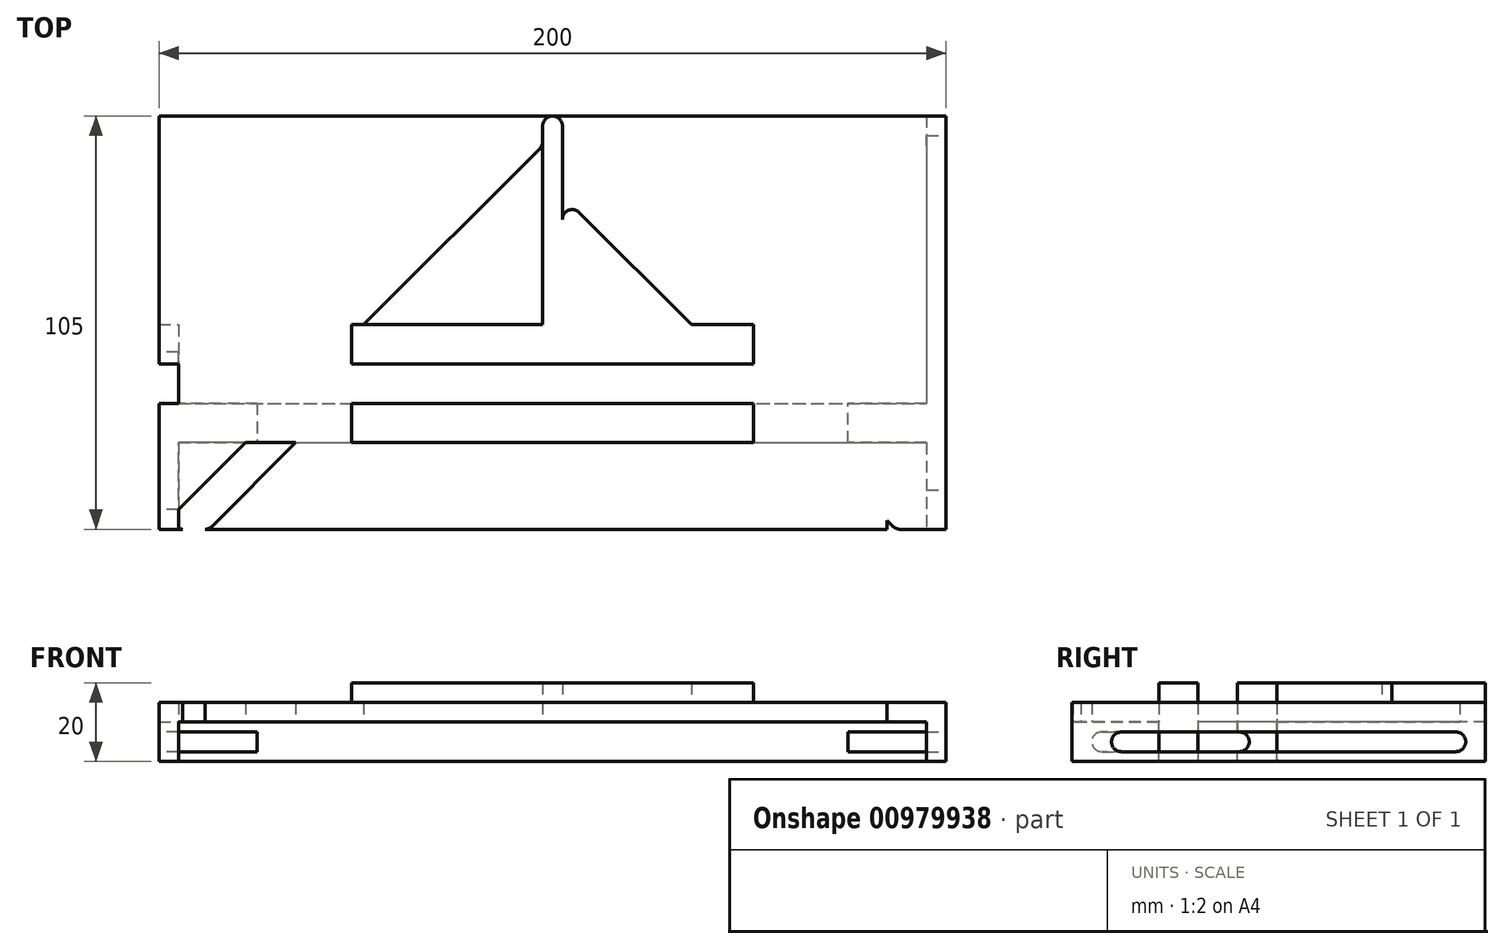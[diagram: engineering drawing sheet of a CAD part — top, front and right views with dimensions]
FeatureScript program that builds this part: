
annotation { "Feature Type Name" : "Feature", "Feature Type Description" : "" }
export const myFeature = defineFeature(function(context is Context, id is Id, definition is map)
    precondition{}
    {
        {
            var Q0;
            Q0=qCreatedBy(makeId("Top.planeOp"),FACE);
            var sketch = newSketch(context, id + "F0", { "sketchPlane" : qUnion([Q0])});
            skLineSegment(sketch, "E0.bottom", {"start": v(-100, 52.5) * mm, "end": v(100, 52.5) * mm});
            skLineSegment(sketch, "E0.top", {"start": v(-100, -52.5) * mm, "end": v(100, -52.5) * mm});
            skLineSegment(sketch, "E0.left", {"start": v(-100, 52.5) * mm, "end": v(-100, -52.5) * mm});
            skLineSegment(sketch, "E0.right", {"start": v(100, 52.5) * mm, "end": v(100, -52.5) * mm});
            skLineSegment(sketch, "E1", {"start": v(95, 52.5) * mm, "end": v(95, -52.5) * mm});
            skLineSegment(sketch, "E2.bottom", {"start": v(0, 52.5) * mm, "end": v(0, 52.5) * mm});
            skLineSegment(sketch, "E2.top", {"start": v(0, -52.5) * mm, "end": v(0, -52.5) * mm});
            skLineSegment(sketch, "E2.left", {"start": v(2.5, 50) * mm, "end": v(2.5, -50) * mm});
            skLineSegment(sketch, "E2.right", {"start": v(-2.5, 50) * mm, "end": v(-2.5, -50) * mm});
            skPoint(sketch, "E3.visualSharp", {"position": v(-2.5, 52.5) * mm});
            skArc(sketch, "E3.filletArc", {"start": v(0, 52.5) * mm, "mid": v(-1.77, 51.77) * mm, "end": v(-2.5, 50) * mm});
            skPoint(sketch, "E4.visualSharp", {"position": v(2.5, 52.5) * mm});
            skArc(sketch, "E4.filletArc", {"start": v(2.5, 50) * mm, "mid": v(1.77, 51.77) * mm, "end": v(0, 52.5) * mm});
            skPoint(sketch, "E5.visualSharp", {"position": v(-2.5, -52.5) * mm});
            skArc(sketch, "E5.filletArc", {"start": v(-2.5, -50) * mm, "mid": v(-1.77, -51.77) * mm, "end": v(0, -52.5) * mm});
            skPoint(sketch, "E6.visualSharp", {"position": v(2.5, -52.5) * mm});
            skArc(sketch, "E6.filletArc", {"start": v(0, -52.5) * mm, "mid": v(1.77, -51.77) * mm, "end": v(2.5, -50) * mm});
            skLineSegment(sketch, "E7", {"start": v(-95.73, -48.23) * mm, "end": v(-3.23, 44.27) * mm});
            skLineSegment(sketch, "E8.0", {"start": v(-86.54, -51.77) * mm, "end": v(-6.77, 28) * mm});
            skLineSegment(sketch, "E9", {"start": v(-2.5, 32.27) * mm, "end": v(-2.5, 0) * mm});
            skLineSegment(sketch, "E10", {"start": v(-2.5, 0) * mm, "end": v(-2.5, 26.24) * mm});
            skPoint(sketch, "E11.visualSharp", {"position": v(-2.5, 32.27) * mm});
            skArc(sketch, "E11.filletArc", {"start": v(-2.5, 26.24) * mm, "mid": v(-4.04, 28.55) * mm, "end": v(-6.77, 28) * mm});
            skLineSegment(sketch, "E12", {"start": v(-2.5, 50) * mm, "end": v(-2.5, 46.04) * mm});
            skPoint(sketch, "E13.visualSharp", {"position": v(-2.5, 45) * mm});
            skArc(sketch, "E13.filletArc", {"start": v(-3.23, 44.27) * mm, "mid": v(-2.7, 45.08) * mm, "end": v(-2.5, 46.04) * mm});
            skLineSegment(sketch, "E14", {"start": v(-93.96, -52.5) * mm, "end": v(-88.3, -52.5) * mm});
            skPoint(sketch, "E15.visualSharp", {"position": v(-100, -52.5) * mm});
            skArc(sketch, "E15.filletArc", {"start": v(-95.73, -48.23) * mm, "mid": v(-96.27, -50.96) * mm, "end": v(-93.96, -52.5) * mm});
            skPoint(sketch, "E16.visualSharp", {"position": v(-87.27, -52.5) * mm});
            skArc(sketch, "E16.filletArc", {"start": v(-88.3, -52.5) * mm, "mid": v(-87.35, -52.3) * mm, "end": v(-86.54, -51.77) * mm});
            skArc(sketch, "E17.MirrorCS", {"start": v(95.73, -48.23) * mm, "mid": v(96.27, -50.96) * mm, "end": v(93.96, -52.5) * mm});
            skLineSegment(sketch, "E18.MirrorCS", {"start": v(93.96, -52.5) * mm, "end": v(88.3, -52.5) * mm});
            skArc(sketch, "E19.MirrorCS", {"start": v(88.3, -52.5) * mm, "mid": v(87.35, -52.3) * mm, "end": v(86.54, -51.77) * mm});
            skLineSegment(sketch, "E20.MirrorCS", {"start": v(95.73, -48.23) * mm, "end": v(3.23, 44.27) * mm});
            skLineSegment(sketch, "E21.MirrorCS", {"start": v(86.54, -51.77) * mm, "end": v(6.77, 28) * mm});
            skArc(sketch, "E22.MirrorCS", {"start": v(2.5, 26.24) * mm, "mid": v(4.04, 28.55) * mm, "end": v(6.77, 28) * mm});
            skArc(sketch, "E23.MirrorCS", {"start": v(3.23, 44.27) * mm, "mid": v(2.7, 45.08) * mm, "end": v(2.5, 46.04) * mm});
            skLineSegment(sketch, "E24", {"start": v(-3.23, 44.27) * mm, "end": v(0, 47.5) * mm, "construction": true});
            skLineSegment(sketch, "E25", {"start": v(3.23, 44.27) * mm, "end": v(0, 47.5) * mm, "construction": true});
            skLineSegment(sketch, "E26.bottom", {"start": v(-48, 65.5) * mm, "end": v(48, 65.5) * mm, "construction": true});
            skLineSegment(sketch, "E26.top", {"start": v(-48, -30.5) * mm, "end": v(48, -30.5) * mm, "construction": true});
            skLineSegment(sketch, "E26.left", {"start": v(-48, 65.5) * mm, "end": v(-48, -30.5) * mm, "construction": true});
            skLineSegment(sketch, "E26.right", {"start": v(48, 65.5) * mm, "end": v(48, -30.5) * mm, "construction": true});
            skLineSegment(sketch, "E27", {"start": v(-48, -25.5) * mm, "end": v(48, -25.5) * mm, "construction": true});
            skLineSegment(sketch, "E28", {"start": v(-48, 2.5) * mm, "end": v(48, 2.5) * mm, "construction": true});
            skLineSegment(sketch, "E29", {"start": v(-48, -0.5) * mm, "end": v(48, -0.5) * mm, "construction": true});
            skLineSegment(sketch, "E30.bottom", {"start": v(-100, -0.5) * mm, "end": v(100, -0.5) * mm});
            skLineSegment(sketch, "E30.top", {"start": v(-100, -30.5) * mm, "end": v(100, -30.5) * mm});
            skLineSegment(sketch, "E30.left", {"start": v(-100, -0.5) * mm, "end": v(-100, -30.5) * mm});
            skLineSegment(sketch, "E30.right", {"start": v(100, -0.5) * mm, "end": v(100, -30.5) * mm});
            skLineSegment(sketch, "E31", {"start": v(-95, -0.5) * mm, "end": v(-95, -30.5) * mm});
            skLineSegment(sketch, "E32", {"start": v(-100, -10.5) * mm, "end": v(100, -10.5) * mm});
            skLineSegment(sketch, "E33", {"start": v(-100, -20.5) * mm, "end": v(100, -20.5) * mm});
            skLineSegment(sketch, "E34", {"start": v(-51, -0.5) * mm, "end": v(-51, -10.5) * mm});
            skLineSegment(sketch, "E35", {"start": v(-51, -10.5) * mm, "end": v(-51, -20.5) * mm, "construction": true});
            skLineSegment(sketch, "E36", {"start": v(-51, -20.5) * mm, "end": v(-51, -30.5) * mm});
            skLineSegment(sketch, "E37", {"start": v(51, -0.5) * mm, "end": v(51, -10.5) * mm});
            skLineSegment(sketch, "E38", {"start": v(51, -10.5) * mm, "end": v(51, -20.5) * mm, "construction": true});
            skLineSegment(sketch, "E39", {"start": v(51, -20.5) * mm, "end": v(51, -30.5) * mm});
            skLineSegment(sketch, "E40", {"start": v(85, 52.5) * mm, "end": v(85, -52.5) * mm});
            skLineSegment(sketch, "E41", {"start": v(-95, -30.5) * mm, "end": v(-95, -52.5) * mm});
            skSolve(sketch);
        }
        {
            var Q0;
            {var subQ0=sQuery(id+"F0.wireOp",EDGE,"E0.right");var subQ1=sQuery(id+"F0.wireOp",EDGE,"E0.bottom");var subQ2=makeQuery(id+"F0.imprint","INTERSECT",VERTEX,{"derivedFrom":[subQ1,subQ0]});Q0=makeQuery(id+"F0.imprint","IMPRINT",FACE,{"disambiguationData":[TD([[makeQuery(id+"F0.imprint","IMPRINT",EDGE,{"disambiguationData":[TD([[subQ2,1.0]])],"derivedFrom":subQ1}),-1.0]])]});}
            var Q1;
            {var subQ10=sQuery(id+"F0.wireOp",EDGE,"E3.filletArc");Q1=makeQuery(id+"F0.imprint","IMPRINT",FACE,{"disambiguationData":[TD([[makeQuery(id+"F0.imprint","IMPRINT",EDGE,{"derivedFrom":subQ10}),-1.0]])]});}
            var Q2;
            {var subQ0=sQuery(id+"F0.wireOp",EDGE,"E4.filletArc");Q2=makeQuery(id+"F0.imprint","IMPRINT",FACE,{"disambiguationData":[TD([[makeQuery(id+"F0.imprint","IMPRINT",EDGE,{"derivedFrom":subQ0}),-1.0]])]});}
            var Q3;
            Q3=makeQuery(id+"F0.imprint","IMPRINT",FACE,{"disambiguationData":[TD([[makeQuery(id+"F0.imprint","IMPRINT",EDGE,{"derivedFrom":sQuery(id+"F0.wireOp",EDGE,"E3.filletArc")}),1.0]])]});
            var Q4;
            {var subQ0=sQuery(id+"F0.wireOp",EDGE,"E9");Q4=makeQuery(id+"F0.imprint","IMPRINT",FACE,{"disambiguationData":[TD([[makeQuery(id+"F0.imprint","IMPRINT",EDGE,{"derivedFrom":subQ0}),-1.0]])]});}
            var Q5;
            {var subQ1=sQuery(id+"F0.wireOp",EDGE,"E10");Q5=makeQuery(id+"F0.imprint","IMPRINT",FACE,{"disambiguationData":[TD([[makeQuery(id+"F0.imprint","IMPRINT",EDGE,{"derivedFrom":subQ1}),1.0]])]});}
            var Q6;
            {var subQ0=sQuery(id+"F0.wireOp",EDGE,"E22.MirrorCS");Q6=makeQuery(id+"F0.imprint","IMPRINT",FACE,{"disambiguationData":[TD([[makeQuery(id+"F0.imprint","IMPRINT",EDGE,{"derivedFrom":subQ0}),-1.0]])]});}
            var Q7;
            {var subQ0=sQuery(id+"F0.wireOp",EDGE,"E22.MirrorCS");Q7=makeQuery(id+"F0.imprint","IMPRINT",FACE,{"disambiguationData":[TD([[makeQuery(id+"F0.imprint","IMPRINT",EDGE,{"derivedFrom":subQ0}),1.0]])]});}
            var Q8;
            {var subQ0=sQuery(id+"F0.wireOp",EDGE,"E1");var subQ1=sQuery(id+"F0.wireOp",EDGE,"E0.bottom");var subQ2=makeQuery(id+"F0.imprint","INTERSECT",VERTEX,{"derivedFrom":[subQ1,subQ0]});Q8=makeQuery(id+"F0.imprint","IMPRINT",FACE,{"disambiguationData":[TD([[makeQuery(id+"F0.imprint","IMPRINT",EDGE,{"disambiguationData":[TD([[subQ2,1.0]])],"derivedFrom":subQ1}),-1.0]])]});}
            var Q9;
            {var subQ0=sQuery(id+"F0.wireOp",EDGE,"E30.bottom");var subQ1=sQuery(id+"F0.wireOp",EDGE,"E1");var subQ2=makeQuery(id+"F0.imprint","INTERSECT",VERTEX,{"derivedFrom":[subQ1,subQ0]});Q9=makeQuery(id+"F0.imprint","IMPRINT",FACE,{"disambiguationData":[TD([[makeQuery(id+"F0.imprint","IMPRINT",EDGE,{"disambiguationData":[TD([[subQ2,-1.0]])],"derivedFrom":subQ1}),-1.0]])]});}
            var Q10;
            {var subQ0=sQuery(id+"F0.wireOp",EDGE,"E32");var subQ1=sQuery(id+"F0.wireOp",EDGE,"E1");var subQ2=makeQuery(id+"F0.imprint","INTERSECT",VERTEX,{"derivedFrom":[subQ1,subQ0]});Q10=makeQuery(id+"F0.imprint","IMPRINT",FACE,{"disambiguationData":[TD([[makeQuery(id+"F0.imprint","IMPRINT",EDGE,{"disambiguationData":[TD([[subQ2,-1.0]])],"derivedFrom":subQ1}),-1.0]])]});}
            var Q11;
            {var subQ0=sQuery(id+"F0.wireOp",EDGE,"E33");var subQ1=sQuery(id+"F0.wireOp",EDGE,"E1");var subQ2=makeQuery(id+"F0.imprint","INTERSECT",VERTEX,{"derivedFrom":[subQ1,subQ0]});Q11=makeQuery(id+"F0.imprint","IMPRINT",FACE,{"disambiguationData":[TD([[makeQuery(id+"F0.imprint","IMPRINT",EDGE,{"disambiguationData":[TD([[subQ2,-1.0]])],"derivedFrom":subQ1}),-1.0]])]});}
            var Q12;
            {var subQ0=sQuery(id+"F0.wireOp",EDGE,"E33");var subQ1=sQuery(id+"F0.wireOp",EDGE,"E1");var subQ2=makeQuery(id+"F0.imprint","INTERSECT",VERTEX,{"derivedFrom":[subQ1,subQ0]});Q12=makeQuery(id+"F0.imprint","IMPRINT",FACE,{"disambiguationData":[TD([[makeQuery(id+"F0.imprint","IMPRINT",EDGE,{"disambiguationData":[TD([[subQ2,-1.0]])],"derivedFrom":subQ1}),1.0]])]});}
            var Q13;
            {var subQ0=sQuery(id+"F0.wireOp",EDGE,"E32");var subQ1=sQuery(id+"F0.wireOp",EDGE,"E1");var subQ2=makeQuery(id+"F0.imprint","INTERSECT",VERTEX,{"derivedFrom":[subQ1,subQ0]});Q13=makeQuery(id+"F0.imprint","IMPRINT",FACE,{"disambiguationData":[TD([[makeQuery(id+"F0.imprint","IMPRINT",EDGE,{"disambiguationData":[TD([[subQ2,-1.0]])],"derivedFrom":subQ1}),1.0]])]});}
            var Q14;
            {var subQ0=sQuery(id+"F0.wireOp",EDGE,"E30.bottom");var subQ1=sQuery(id+"F0.wireOp",EDGE,"E1");var subQ2=makeQuery(id+"F0.imprint","INTERSECT",VERTEX,{"derivedFrom":[subQ1,subQ0]});Q14=makeQuery(id+"F0.imprint","IMPRINT",FACE,{"disambiguationData":[TD([[makeQuery(id+"F0.imprint","IMPRINT",EDGE,{"disambiguationData":[TD([[subQ2,-1.0]])],"derivedFrom":subQ1}),1.0]])]});}
            var Q15;
            {var subQ0=sQuery(id+"F0.wireOp",EDGE,"E30.top");var subQ1=sQuery(id+"F0.wireOp",EDGE,"E1");var subQ2=makeQuery(id+"F0.imprint","INTERSECT",VERTEX,{"derivedFrom":[subQ1,subQ0]});Q15=makeQuery(id+"F0.imprint","IMPRINT",FACE,{"disambiguationData":[TD([[makeQuery(id+"F0.imprint","IMPRINT",EDGE,{"disambiguationData":[TD([[subQ2,-1.0]])],"derivedFrom":subQ1}),-1.0]])]});}
            var Q16;
            {var subQ1=sQuery(id+"F0.wireOp",EDGE,"E0.top");var subQ5=sQuery(id+"F0.wireOp",EDGE,"E0.right");var subQ6=makeQuery(id+"F0.imprint","INTERSECT",VERTEX,{"derivedFrom":[subQ1,subQ5]});Q16=makeQuery(id+"F0.imprint","IMPRINT",FACE,{"disambiguationData":[TD([[makeQuery(id+"F0.imprint","IMPRINT",EDGE,{"disambiguationData":[TD([[subQ6,1.0]])],"derivedFrom":subQ1}),1.0]])]});}
            var Q17;
            {var subQ1=sQuery(id+"F0.wireOp",EDGE,"E18.MirrorCS");Q17=makeQuery(id+"F0.imprint","IMPRINT",FACE,{"disambiguationData":[TD([[makeQuery(id+"F0.imprint","IMPRINT",EDGE,{"derivedFrom":subQ1}),-1.0]])]});}
            var Q18;
            {var subQ0=sQuery(id+"F0.wireOp",EDGE,"E19.MirrorCS");Q18=makeQuery(id+"F0.imprint","IMPRINT",FACE,{"disambiguationData":[TD([[makeQuery(id+"F0.imprint","IMPRINT",EDGE,{"derivedFrom":subQ0}),1.0]])]});}
            var Q19;
            {var subQ0=sQuery(id+"F0.wireOp",EDGE,"E20.MirrorCS");var subQ1=sQuery(id+"F0.wireOp",EDGE,"E1");var subQ2=makeQuery(id+"F0.imprint","INTERSECT",VERTEX,{"derivedFrom":[subQ1,subQ0]});Q19=makeQuery(id+"F0.imprint","IMPRINT",FACE,{"disambiguationData":[TD([[makeQuery(id+"F0.imprint","IMPRINT",EDGE,{"disambiguationData":[TD([[subQ2,-1.0]])],"derivedFrom":subQ1}),1.0]])]});}
            var Q20;
            {var subQ0=sQuery(id+"F0.wireOp",EDGE,"E1");var subQ1=sQuery(id+"F0.wireOp",EDGE,"E0.top");var subQ2=makeQuery(id+"F0.imprint","INTERSECT",VERTEX,{"derivedFrom":[subQ1,subQ0]});Q20=makeQuery(id+"F0.imprint","IMPRINT",FACE,{"disambiguationData":[TD([[makeQuery(id+"F0.imprint","IMPRINT",EDGE,{"disambiguationData":[TD([[subQ2,1.0]])],"derivedFrom":subQ0}),-1.0]])]});}
            extrude(context, id + "F1", {"entities" : qUnion([Q0, Q1, Q2, Q3, Q4, Q5, Q6, Q7, Q8, Q9, Q10, Q11, Q12, Q13, Q14, Q15, Q16, Q17, Q18, Q19, Q20]), "depth" : 5 * mm, "offsetDistance" : 25 * mm});
        }
        {
            var Q0;
            {var subQ0=sQuery(id+"F0.wireOp",EDGE,"E22.MirrorCS");Q0=makeQuery(id+"F0.imprint","IMPRINT",FACE,{"disambiguationData":[TD([[makeQuery(id+"F0.imprint","IMPRINT",EDGE,{"derivedFrom":subQ0}),1.0]])]});}
            var Q1;
            Q1=makeQuery(id+"F0.imprint","IMPRINT",FACE,{"disambiguationData":[TD([[makeQuery(id+"F0.imprint","IMPRINT",EDGE,{"derivedFrom":sQuery(id+"F0.wireOp",EDGE,"E3.filletArc")}),1.0]])]});
            var Q2;
            {var subQ0=sQuery(id+"F0.wireOp",EDGE,"E9");Q2=makeQuery(id+"F0.imprint","IMPRINT",FACE,{"disambiguationData":[TD([[makeQuery(id+"F0.imprint","IMPRINT",EDGE,{"derivedFrom":subQ0}),-1.0]])]});}
            extrude(context, id + "F2", {"entities" : qUnion([Q0, Q1, Q2]), "operationType" : NewBodyOperationType.ADD, "depth" : 10 * mm, "offsetDistance" : 25 * mm});
        }
        {
            var Q0;
            {var subQ0=sQuery(id+"F0.wireOp",EDGE,"E0.right");var subQ1=sQuery(id+"F0.wireOp",EDGE,"E0.bottom");var subQ2=makeQuery(id+"F0.imprint","INTERSECT",VERTEX,{"derivedFrom":[subQ1,subQ0]});Q0=makeQuery(id+"F0.imprint","IMPRINT",FACE,{"disambiguationData":[TD([[makeQuery(id+"F0.imprint","IMPRINT",EDGE,{"disambiguationData":[TD([[subQ2,1.0]])],"derivedFrom":subQ1}),-1.0]])]});}
            var Q1;
            {var subQ0=sQuery(id+"F0.wireOp",EDGE,"E30.bottom");var subQ1=sQuery(id+"F0.wireOp",EDGE,"E1");var subQ2=makeQuery(id+"F0.imprint","INTERSECT",VERTEX,{"derivedFrom":[subQ1,subQ0]});Q1=makeQuery(id+"F0.imprint","IMPRINT",FACE,{"disambiguationData":[TD([[makeQuery(id+"F0.imprint","IMPRINT",EDGE,{"disambiguationData":[TD([[subQ2,-1.0]])],"derivedFrom":subQ1}),1.0]])]});}
            var Q2;
            {var subQ0=sQuery(id+"F0.wireOp",EDGE,"E32");var subQ1=sQuery(id+"F0.wireOp",EDGE,"E1");var subQ2=makeQuery(id+"F0.imprint","INTERSECT",VERTEX,{"derivedFrom":[subQ1,subQ0]});Q2=makeQuery(id+"F0.imprint","IMPRINT",FACE,{"disambiguationData":[TD([[makeQuery(id+"F0.imprint","IMPRINT",EDGE,{"disambiguationData":[TD([[subQ2,-1.0]])],"derivedFrom":subQ1}),1.0]])]});}
            var Q3;
            {var subQ0=sQuery(id+"F0.wireOp",EDGE,"E33");var subQ1=sQuery(id+"F0.wireOp",EDGE,"E1");var subQ2=makeQuery(id+"F0.imprint","INTERSECT",VERTEX,{"derivedFrom":[subQ1,subQ0]});Q3=makeQuery(id+"F0.imprint","IMPRINT",FACE,{"disambiguationData":[TD([[makeQuery(id+"F0.imprint","IMPRINT",EDGE,{"disambiguationData":[TD([[subQ2,-1.0]])],"derivedFrom":subQ1}),1.0]])]});}
            var Q4;
            {var subQ1=sQuery(id+"F0.wireOp",EDGE,"E0.top");var subQ5=sQuery(id+"F0.wireOp",EDGE,"E0.right");var subQ6=makeQuery(id+"F0.imprint","INTERSECT",VERTEX,{"derivedFrom":[subQ1,subQ5]});Q4=makeQuery(id+"F0.imprint","IMPRINT",FACE,{"disambiguationData":[TD([[makeQuery(id+"F0.imprint","IMPRINT",EDGE,{"disambiguationData":[TD([[subQ6,1.0]])],"derivedFrom":subQ1}),1.0]])]});}
            var Q5;
            {var subQ0=sQuery(id+"F0.wireOp",EDGE,"E20.MirrorCS");var subQ1=sQuery(id+"F0.wireOp",EDGE,"E1");var subQ2=makeQuery(id+"F0.imprint","INTERSECT",VERTEX,{"derivedFrom":[subQ1,subQ0]});Q5=makeQuery(id+"F0.imprint","IMPRINT",FACE,{"disambiguationData":[TD([[makeQuery(id+"F0.imprint","IMPRINT",EDGE,{"disambiguationData":[TD([[subQ2,-1.0]])],"derivedFrom":subQ1}),1.0]])]});}
            extrude(context, id + "F3", {"entities" : qUnion([Q0, Q1, Q2, Q3, Q4, Q5]), "operationType" : NewBodyOperationType.ADD, "oppositeDirection" : true, "depth" : 10 * mm, "offsetDistance" : 25 * mm});
        }
        {
            var Q0;
            {var subQ1=sQuery(id+"F0.wireOp",EDGE,"E30.top");var subQ3=sQuery(id+"F0.wireOp",EDGE,"E31");var subQ4=makeQuery(id+"F0.imprint","INTERSECT",VERTEX,{"derivedFrom":[subQ1,subQ3]});Q0=makeQuery(id+"F0.imprint","IMPRINT",FACE,{"disambiguationData":[TD([[makeQuery(id+"F0.imprint","IMPRINT",EDGE,{"disambiguationData":[TD([[subQ4,1.0]])],"derivedFrom":subQ3}),-1.0]])]});}
            var Q1;
            {var subQ0=sQuery(id+"F0.wireOp",EDGE,"E30.top");var subQ1=sQuery(id+"F0.wireOp",EDGE,"E7");var subQ2=makeQuery(id+"F0.imprint","INTERSECT",VERTEX,{"derivedFrom":[subQ1,subQ0]});Q1=makeQuery(id+"F0.imprint","IMPRINT",FACE,{"disambiguationData":[TD([[makeQuery(id+"F0.imprint","IMPRINT",EDGE,{"disambiguationData":[TD([[subQ2,-1.0]])],"derivedFrom":subQ1}),1.0]])]});}
            var Q2;
            {var subQ0=sQuery(id+"F0.wireOp",EDGE,"E32");var subQ1=sQuery(id+"F0.wireOp",EDGE,"E30.left");var subQ2=makeQuery(id+"F0.imprint","INTERSECT",VERTEX,{"derivedFrom":[subQ1,subQ0]});Q2=makeQuery(id+"F0.imprint","IMPRINT",FACE,{"disambiguationData":[TD([[makeQuery(id+"F0.imprint","IMPRINT",EDGE,{"disambiguationData":[TD([[subQ2,-1.0]])],"derivedFrom":subQ1}),1.0]])]});}
            var Q3;
            {var subQ1=sQuery(id+"F0.wireOp",EDGE,"E30.bottom");var subQ3=sQuery(id+"F0.wireOp",EDGE,"E31");var subQ4=makeQuery(id+"F0.imprint","INTERSECT",VERTEX,{"derivedFrom":[subQ1,subQ3]});Q3=makeQuery(id+"F0.imprint","IMPRINT",FACE,{"disambiguationData":[TD([[makeQuery(id+"F0.imprint","IMPRINT",EDGE,{"disambiguationData":[TD([[subQ4,-1.0]])],"derivedFrom":subQ3}),-1.0]])]});}
            var Q4;
            {var subQ0=sQuery(id+"F0.wireOp",EDGE,"E32");var subQ1=sQuery(id+"F0.wireOp",EDGE,"E7");var subQ2=makeQuery(id+"F0.imprint","INTERSECT",VERTEX,{"derivedFrom":[subQ1,subQ0]});Q4=makeQuery(id+"F0.imprint","IMPRINT",FACE,{"disambiguationData":[TD([[makeQuery(id+"F0.imprint","IMPRINT",EDGE,{"disambiguationData":[TD([[subQ2,-1.0]])],"derivedFrom":subQ1}),1.0]])]});}
            var Q5;
            {var subQ0=sQuery(id+"F0.wireOp",EDGE,"E33");var subQ1=sQuery(id+"F0.wireOp",EDGE,"E7");var subQ2=makeQuery(id+"F0.imprint","INTERSECT",VERTEX,{"derivedFrom":[subQ1,subQ0]});Q5=makeQuery(id+"F0.imprint","IMPRINT",FACE,{"disambiguationData":[TD([[makeQuery(id+"F0.imprint","IMPRINT",EDGE,{"disambiguationData":[TD([[subQ2,-1.0]])],"derivedFrom":subQ1}),1.0]])]});}
            var Q6;
            {var subQ0=sQuery(id+"F0.wireOp",EDGE,"E30.top");var subQ1=sQuery(id+"F0.wireOp",EDGE,"E7");var subQ2=makeQuery(id+"F0.imprint","INTERSECT",VERTEX,{"derivedFrom":[subQ1,subQ0]});Q6=makeQuery(id+"F0.imprint","IMPRINT",FACE,{"disambiguationData":[TD([[makeQuery(id+"F0.imprint","IMPRINT",EDGE,{"disambiguationData":[TD([[subQ2,-1.0]])],"derivedFrom":subQ1}),-1.0]])]});}
            var Q7;
            {var subQ4=sQuery(id+"F0.wireOp",EDGE,"E7");var subQ6=sQuery(id+"F0.wireOp",EDGE,"E33");var subQ7=makeQuery(id+"F0.imprint","INTERSECT",VERTEX,{"derivedFrom":[subQ4,subQ6]});Q7=makeQuery(id+"F0.imprint","IMPRINT",FACE,{"disambiguationData":[TD([[makeQuery(id+"F0.imprint","IMPRINT",EDGE,{"disambiguationData":[TD([[subQ7,-1.0]])],"derivedFrom":subQ4}),-1.0]])]});}
            var Q8;
            {var subQ0=sQuery(id+"F0.wireOp",EDGE,"E34");var subQ6=sQuery(id+"F0.wireOp",EDGE,"E7");var subQ9=makeQuery(id+"F0.imprint","INTERSECT",VERTEX,{"derivedFrom":[subQ6,subQ0]});Q8=makeQuery(id+"F0.imprint","IMPRINT",FACE,{"disambiguationData":[TD([[makeQuery(id+"F0.imprint","IMPRINT",EDGE,{"disambiguationData":[TD([[subQ9,-1.0]])],"derivedFrom":subQ6}),-1.0]])]});}
            var Q9;
            {var subQ0=sQuery(id+"F0.wireOp",EDGE,"E32");var subQ1=sQuery(id+"F0.wireOp",EDGE,"E7");var subQ2=makeQuery(id+"F0.imprint","INTERSECT",VERTEX,{"derivedFrom":[subQ1,subQ0]});Q9=makeQuery(id+"F0.imprint","IMPRINT",FACE,{"disambiguationData":[TD([[makeQuery(id+"F0.imprint","IMPRINT",EDGE,{"disambiguationData":[TD([[subQ2,-1.0]])],"derivedFrom":subQ1}),-1.0]])]});}
            var Q10;
            {var subQ0=sQuery(id+"F0.wireOp",EDGE,"E34");var subQ1=sQuery(id+"F0.wireOp",EDGE,"E7");var subQ2=makeQuery(id+"F0.imprint","INTERSECT",VERTEX,{"derivedFrom":[subQ1,subQ0]});Q10=makeQuery(id+"F0.imprint","IMPRINT",FACE,{"disambiguationData":[TD([[makeQuery(id+"F0.imprint","IMPRINT",EDGE,{"disambiguationData":[TD([[subQ2,-1.0]])],"derivedFrom":subQ1}),1.0]])]});}
            var Q11;
            {var subQ0=sQuery(id+"F0.wireOp",EDGE,"E30.bottom");var subQ1=sQuery(id+"F0.wireOp",EDGE,"E2.right");var subQ2=makeQuery(id+"F0.imprint","INTERSECT",VERTEX,{"derivedFrom":[subQ1,subQ0]});Q11=makeQuery(id+"F0.imprint","IMPRINT",FACE,{"disambiguationData":[TD([[makeQuery(id+"F0.imprint","IMPRINT",EDGE,{"disambiguationData":[TD([[subQ2,-1.0]])],"derivedFrom":subQ1}),-1.0]])]});}
            var Q12;
            {var subQ4=sQuery(id+"F0.wireOp",EDGE,"E32");var subQ5=sQuery(id+"F0.wireOp",EDGE,"E2.right");var subQ6=makeQuery(id+"F0.imprint","INTERSECT",VERTEX,{"derivedFrom":[subQ5,subQ4]});Q12=makeQuery(id+"F0.imprint","IMPRINT",FACE,{"disambiguationData":[TD([[makeQuery(id+"F0.imprint","IMPRINT",EDGE,{"disambiguationData":[TD([[subQ6,-1.0]])],"derivedFrom":subQ5}),-1.0]])]});}
            var Q13;
            {var subQ5=sQuery(id+"F0.wireOp",EDGE,"E36");Q13=makeQuery(id+"F0.imprint","IMPRINT",FACE,{"disambiguationData":[TD([[makeQuery(id+"F0.imprint","IMPRINT",EDGE,{"derivedFrom":subQ5}),-1.0]])]});}
            var Q14;
            {var subQ5=sQuery(id+"F0.wireOp",EDGE,"E36");Q14=makeQuery(id+"F0.imprint","IMPRINT",FACE,{"disambiguationData":[TD([[makeQuery(id+"F0.imprint","IMPRINT",EDGE,{"derivedFrom":subQ5}),1.0]])]});}
            var Q15;
            {var subQ0=sQuery(id+"F0.wireOp",EDGE,"E30.bottom");var subQ1=sQuery(id+"F0.wireOp",EDGE,"E2.left");var subQ2=makeQuery(id+"F0.imprint","INTERSECT",VERTEX,{"derivedFrom":[subQ1,subQ0]});Q15=makeQuery(id+"F0.imprint","IMPRINT",FACE,{"disambiguationData":[TD([[makeQuery(id+"F0.imprint","IMPRINT",EDGE,{"disambiguationData":[TD([[subQ2,-1.0]])],"derivedFrom":subQ1}),-1.0]])]});}
            var Q16;
            {var subQ0=sQuery(id+"F0.wireOp",EDGE,"E32");var subQ1=sQuery(id+"F0.wireOp",EDGE,"E2.left");var subQ2=makeQuery(id+"F0.imprint","INTERSECT",VERTEX,{"derivedFrom":[subQ1,subQ0]});Q16=makeQuery(id+"F0.imprint","IMPRINT",FACE,{"disambiguationData":[TD([[makeQuery(id+"F0.imprint","IMPRINT",EDGE,{"disambiguationData":[TD([[subQ2,-1.0]])],"derivedFrom":subQ1}),-1.0]])]});}
            var Q17;
            {var subQ0=sQuery(id+"F0.wireOp",EDGE,"E33");var subQ1=sQuery(id+"F0.wireOp",EDGE,"E2.left");var subQ2=makeQuery(id+"F0.imprint","INTERSECT",VERTEX,{"derivedFrom":[subQ1,subQ0]});Q17=makeQuery(id+"F0.imprint","IMPRINT",FACE,{"disambiguationData":[TD([[makeQuery(id+"F0.imprint","IMPRINT",EDGE,{"disambiguationData":[TD([[subQ2,-1.0]])],"derivedFrom":subQ1}),-1.0]])]});}
            var Q18;
            {var subQ2=sQuery(id+"F0.wireOp",EDGE,"E2.left");var subQ4=sQuery(id+"F0.wireOp",EDGE,"E32");var subQ5=makeQuery(id+"F0.imprint","INTERSECT",VERTEX,{"derivedFrom":[subQ2,subQ4]});Q18=makeQuery(id+"F0.imprint","IMPRINT",FACE,{"disambiguationData":[TD([[makeQuery(id+"F0.imprint","IMPRINT",EDGE,{"disambiguationData":[TD([[subQ5,-1.0]])],"derivedFrom":subQ2}),1.0]])]});}
            var Q19;
            {var subQ0=sQuery(id+"F0.wireOp",EDGE,"E30.bottom");var subQ1=sQuery(id+"F0.wireOp",EDGE,"E2.left");var subQ2=makeQuery(id+"F0.imprint","INTERSECT",VERTEX,{"derivedFrom":[subQ1,subQ0]});Q19=makeQuery(id+"F0.imprint","IMPRINT",FACE,{"disambiguationData":[TD([[makeQuery(id+"F0.imprint","IMPRINT",EDGE,{"disambiguationData":[TD([[subQ2,-1.0]])],"derivedFrom":subQ1}),1.0]])]});}
            var Q20;
            {var subQ5=sQuery(id+"F0.wireOp",EDGE,"E39");Q20=makeQuery(id+"F0.imprint","IMPRINT",FACE,{"disambiguationData":[TD([[makeQuery(id+"F0.imprint","IMPRINT",EDGE,{"derivedFrom":subQ5}),1.0]])]});}
            var Q21;
            {var subQ0=sQuery(id+"F0.wireOp",EDGE,"E30.top");var subQ1=sQuery(id+"F0.wireOp",EDGE,"E20.MirrorCS");var subQ2=makeQuery(id+"F0.imprint","INTERSECT",VERTEX,{"derivedFrom":[subQ1,subQ0]});Q21=makeQuery(id+"F0.imprint","IMPRINT",FACE,{"disambiguationData":[TD([[makeQuery(id+"F0.imprint","IMPRINT",EDGE,{"disambiguationData":[TD([[subQ2,-1.0]])],"derivedFrom":subQ1}),1.0]])]});}
            var Q22;
            {var subQ4=sQuery(id+"F0.wireOp",EDGE,"E33");var subQ6=sQuery(id+"F0.wireOp",EDGE,"E20.MirrorCS");var subQ8=makeQuery(id+"F0.imprint","INTERSECT",VERTEX,{"derivedFrom":[subQ6,subQ4]});Q22=makeQuery(id+"F0.imprint","IMPRINT",FACE,{"disambiguationData":[TD([[makeQuery(id+"F0.imprint","IMPRINT",EDGE,{"disambiguationData":[TD([[subQ8,-1.0]])],"derivedFrom":subQ6}),1.0]])]});}
            var Q23;
            {var subQ5=sQuery(id+"F0.wireOp",EDGE,"E39");Q23=makeQuery(id+"F0.imprint","IMPRINT",FACE,{"disambiguationData":[TD([[makeQuery(id+"F0.imprint","IMPRINT",EDGE,{"derivedFrom":subQ5}),-1.0]])]});}
            var Q24;
            {var subQ0=sQuery(id+"F0.wireOp",EDGE,"E37");var subQ6=sQuery(id+"F0.wireOp",EDGE,"E20.MirrorCS");var subQ9=makeQuery(id+"F0.imprint","INTERSECT",VERTEX,{"derivedFrom":[subQ6,subQ0]});Q24=makeQuery(id+"F0.imprint","IMPRINT",FACE,{"disambiguationData":[TD([[makeQuery(id+"F0.imprint","IMPRINT",EDGE,{"disambiguationData":[TD([[subQ9,-1.0]])],"derivedFrom":subQ6}),1.0]])]});}
            var Q25;
            {var subQ0=sQuery(id+"F0.wireOp",EDGE,"E37");var subQ1=sQuery(id+"F0.wireOp",EDGE,"E20.MirrorCS");var subQ2=makeQuery(id+"F0.imprint","INTERSECT",VERTEX,{"derivedFrom":[subQ1,subQ0]});Q25=makeQuery(id+"F0.imprint","IMPRINT",FACE,{"disambiguationData":[TD([[makeQuery(id+"F0.imprint","IMPRINT",EDGE,{"disambiguationData":[TD([[subQ2,-1.0]])],"derivedFrom":subQ1}),-1.0]])]});}
            var Q26;
            {var subQ0=sQuery(id+"F0.wireOp",EDGE,"E32");var subQ1=sQuery(id+"F0.wireOp",EDGE,"E20.MirrorCS");var subQ2=makeQuery(id+"F0.imprint","INTERSECT",VERTEX,{"derivedFrom":[subQ1,subQ0]});Q26=makeQuery(id+"F0.imprint","IMPRINT",FACE,{"disambiguationData":[TD([[makeQuery(id+"F0.imprint","IMPRINT",EDGE,{"disambiguationData":[TD([[subQ2,-1.0]])],"derivedFrom":subQ1}),1.0]])]});}
            var Q27;
            {var subQ0=sQuery(id+"F0.wireOp",EDGE,"E30.top");var subQ1=sQuery(id+"F0.wireOp",EDGE,"E20.MirrorCS");var subQ2=makeQuery(id+"F0.imprint","INTERSECT",VERTEX,{"derivedFrom":[subQ1,subQ0]});Q27=makeQuery(id+"F0.imprint","IMPRINT",FACE,{"disambiguationData":[TD([[makeQuery(id+"F0.imprint","IMPRINT",EDGE,{"disambiguationData":[TD([[subQ2,-1.0]])],"derivedFrom":subQ1}),-1.0]])]});}
            var Q28;
            {var subQ0=sQuery(id+"F0.wireOp",EDGE,"E33");var subQ1=sQuery(id+"F0.wireOp",EDGE,"E20.MirrorCS");var subQ2=makeQuery(id+"F0.imprint","INTERSECT",VERTEX,{"derivedFrom":[subQ1,subQ0]});Q28=makeQuery(id+"F0.imprint","IMPRINT",FACE,{"disambiguationData":[TD([[makeQuery(id+"F0.imprint","IMPRINT",EDGE,{"disambiguationData":[TD([[subQ2,-1.0]])],"derivedFrom":subQ1}),-1.0]])]});}
            var Q29;
            {var subQ3=sQuery(id+"F0.wireOp",EDGE,"E20.MirrorCS");var subQ5=sQuery(id+"F0.wireOp",EDGE,"E32");var subQ6=makeQuery(id+"F0.imprint","INTERSECT",VERTEX,{"derivedFrom":[subQ3,subQ5]});Q29=makeQuery(id+"F0.imprint","IMPRINT",FACE,{"disambiguationData":[TD([[makeQuery(id+"F0.imprint","IMPRINT",EDGE,{"disambiguationData":[TD([[subQ6,-1.0]])],"derivedFrom":subQ3}),-1.0]])]});}
            var Q30;
            {var subQ0=sQuery(id+"F0.wireOp",EDGE,"E40");var subQ1=sQuery(id+"F0.wireOp",EDGE,"E20.MirrorCS");var subQ2=makeQuery(id+"F0.imprint","INTERSECT",VERTEX,{"derivedFrom":[subQ1,subQ0]});Q30=makeQuery(id+"F0.imprint","IMPRINT",FACE,{"disambiguationData":[TD([[makeQuery(id+"F0.imprint","IMPRINT",EDGE,{"disambiguationData":[TD([[subQ2,-1.0]])],"derivedFrom":subQ1}),-1.0]])]});}
            var Q31;
            {var subQ0=sQuery(id+"F0.wireOp",EDGE,"E40");var subQ1=sQuery(id+"F0.wireOp",EDGE,"E20.MirrorCS");var subQ2=makeQuery(id+"F0.imprint","INTERSECT",VERTEX,{"derivedFrom":[subQ1,subQ0]});Q31=makeQuery(id+"F0.imprint","IMPRINT",FACE,{"disambiguationData":[TD([[makeQuery(id+"F0.imprint","IMPRINT",EDGE,{"disambiguationData":[TD([[subQ2,-1.0]])],"derivedFrom":subQ1}),1.0]])]});}
            var Q32;
            {var subQ5=sQuery(id+"F0.wireOp",EDGE,"E6.filletArc");Q32=makeQuery(id+"F0.imprint","IMPRINT",FACE,{"disambiguationData":[TD([[makeQuery(id+"F0.imprint","IMPRINT",EDGE,{"derivedFrom":subQ5}),-1.0]])]});}
            var Q33;
            {var subQ0=sQuery(id+"F0.wireOp",EDGE,"E5.filletArc");Q33=makeQuery(id+"F0.imprint","IMPRINT",FACE,{"disambiguationData":[TD([[makeQuery(id+"F0.imprint","IMPRINT",EDGE,{"derivedFrom":subQ0}),1.0]])]});}
            var Q34;
            {var subQ4=sQuery(id+"F0.wireOp",EDGE,"E5.filletArc");Q34=makeQuery(id+"F0.imprint","IMPRINT",FACE,{"disambiguationData":[TD([[makeQuery(id+"F0.imprint","IMPRINT",EDGE,{"derivedFrom":subQ4}),-1.0]])]});}
            var Q35;
            Q35=makeQuery(id+"F0.imprint","IMPRINT",FACE,{"disambiguationData":[TD([[makeQuery(id+"F0.imprint","IMPRINT",EDGE,{"derivedFrom":sQuery(id+"F0.wireOp",EDGE,"E14")}),1.0]])]});
            var Q36;
            {var subQ0=sQuery(id+"F0.wireOp",EDGE,"E15.filletArc");Q36=makeQuery(id+"F0.imprint","IMPRINT",FACE,{"disambiguationData":[TD([[makeQuery(id+"F0.imprint","IMPRINT",EDGE,{"derivedFrom":subQ0}),-1.0]])]});}
            var Q37;
            {var subQ0=sQuery(id+"F0.wireOp",EDGE,"E41");var subQ1=sQuery(id+"F0.wireOp",EDGE,"E7");var subQ2=makeQuery(id+"F0.imprint","INTERSECT",VERTEX,{"derivedFrom":[subQ1,subQ0]});Q37=makeQuery(id+"F0.imprint","IMPRINT",FACE,{"disambiguationData":[TD([[makeQuery(id+"F0.imprint","IMPRINT",EDGE,{"disambiguationData":[TD([[subQ2,-1.0]])],"derivedFrom":subQ1}),1.0]])]});}
            var Q38;
            {var subQ5=sQuery(id+"F0.wireOp",EDGE,"E0.left");var subQ6=sQuery(id+"F0.wireOp",EDGE,"E0.top");var subQ7=makeQuery(id+"F0.imprint","INTERSECT",VERTEX,{"derivedFrom":[subQ6,subQ5]});Q38=makeQuery(id+"F0.imprint","IMPRINT",FACE,{"disambiguationData":[TD([[makeQuery(id+"F0.imprint","IMPRINT",EDGE,{"disambiguationData":[TD([[subQ7,-1.0]])],"derivedFrom":subQ6}),1.0]])]});}
            var Q39;
            {var subQ0=sQuery(id+"F0.wireOp",EDGE,"E15.filletArc");var subQ1=sQuery(id+"F0.wireOp",EDGE,"E7");var subQ2=makeQuery(id+"F0.imprint","INTERSECT",VERTEX,{"derivedFrom":[subQ1,subQ0]});Q39=makeQuery(id+"F0.imprint","IMPRINT",FACE,{"disambiguationData":[TD([[makeQuery(id+"F0.imprint","IMPRINT",EDGE,{"disambiguationData":[TD([[subQ2,-1.0]])],"derivedFrom":subQ1}),-1.0]])]});}
            extrude(context, id + "F4", {"entities" : qUnion([Q0, Q1, Q2, Q3, Q4, Q5, Q6, Q7, Q8, Q9, Q10, Q11, Q12, Q13, Q14, Q15, Q16, Q17, Q18, Q19, Q20, Q21, Q22, Q23, Q24, Q25, Q26, Q27, Q28, Q29, Q30, Q31, Q32, Q33, Q34, Q35, Q36, Q37, Q38, Q39]), "depth" : 5 * mm, "offsetDistance" : 25 * mm});
        }
        {
            var Q0;
            {var subQ1=sQuery(id+"F0.wireOp",EDGE,"E30.bottom");var subQ3=sQuery(id+"F0.wireOp",EDGE,"E31");var subQ4=makeQuery(id+"F0.imprint","INTERSECT",VERTEX,{"derivedFrom":[subQ1,subQ3]});Q0=makeQuery(id+"F0.imprint","IMPRINT",FACE,{"disambiguationData":[TD([[makeQuery(id+"F0.imprint","IMPRINT",EDGE,{"disambiguationData":[TD([[subQ4,-1.0]])],"derivedFrom":subQ3}),-1.0]])]});}
            var Q1;
            {var subQ0=sQuery(id+"F0.wireOp",EDGE,"E32");var subQ1=sQuery(id+"F0.wireOp",EDGE,"E30.left");var subQ2=makeQuery(id+"F0.imprint","INTERSECT",VERTEX,{"derivedFrom":[subQ1,subQ0]});Q1=makeQuery(id+"F0.imprint","IMPRINT",FACE,{"disambiguationData":[TD([[makeQuery(id+"F0.imprint","IMPRINT",EDGE,{"disambiguationData":[TD([[subQ2,-1.0]])],"derivedFrom":subQ1}),1.0]])]});}
            var Q2;
            {var subQ0=sQuery(id+"F0.wireOp",EDGE,"E30.left");var subQ5=sQuery(id+"F0.wireOp",EDGE,"E33");var subQ7=makeQuery(id+"F0.imprint","INTERSECT",VERTEX,{"derivedFrom":[subQ0,subQ5]});Q2=makeQuery(id+"F0.imprint","IMPRINT",FACE,{"disambiguationData":[TD([[makeQuery(id+"F0.imprint","IMPRINT",EDGE,{"disambiguationData":[TD([[subQ7,-1.0]])],"derivedFrom":subQ5}),-1.0]])]});}
            var Q3;
            {var subQ5=sQuery(id+"F0.wireOp",EDGE,"E0.left");var subQ6=sQuery(id+"F0.wireOp",EDGE,"E0.top");var subQ7=makeQuery(id+"F0.imprint","INTERSECT",VERTEX,{"derivedFrom":[subQ6,subQ5]});Q3=makeQuery(id+"F0.imprint","IMPRINT",FACE,{"disambiguationData":[TD([[makeQuery(id+"F0.imprint","IMPRINT",EDGE,{"disambiguationData":[TD([[subQ7,-1.0]])],"derivedFrom":subQ6}),1.0]])]});}
            var Q4;
            {var subQ0=sQuery(id+"F0.wireOp",EDGE,"E15.filletArc");var subQ1=sQuery(id+"F0.wireOp",EDGE,"E7");var subQ2=makeQuery(id+"F0.imprint","INTERSECT",VERTEX,{"derivedFrom":[subQ1,subQ0]});Q4=makeQuery(id+"F0.imprint","IMPRINT",FACE,{"disambiguationData":[TD([[makeQuery(id+"F0.imprint","IMPRINT",EDGE,{"disambiguationData":[TD([[subQ2,-1.0]])],"derivedFrom":subQ1}),-1.0]])]});}
            extrude(context, id + "F5", {"entities" : qUnion([Q0, Q1, Q2, Q3, Q4]), "operationType" : NewBodyOperationType.ADD, "oppositeDirection" : true, "depth" : 10 * mm, "offsetDistance" : 25 * mm});
        }
        {
            var Q0;
            {var subQ0=sQuery(id+"F0.wireOp",EDGE,"E30.bottom");var subQ1=sQuery(id+"F0.wireOp",EDGE,"E2.right");var subQ2=makeQuery(id+"F0.imprint","INTERSECT",VERTEX,{"derivedFrom":[subQ1,subQ0]});Q0=makeQuery(id+"F0.imprint","IMPRINT",FACE,{"disambiguationData":[TD([[makeQuery(id+"F0.imprint","IMPRINT",EDGE,{"disambiguationData":[TD([[subQ2,-1.0]])],"derivedFrom":subQ1}),-1.0]])]});}
            var Q1;
            {var subQ0=sQuery(id+"F0.wireOp",EDGE,"E34");var subQ6=sQuery(id+"F0.wireOp",EDGE,"E7");var subQ9=makeQuery(id+"F0.imprint","INTERSECT",VERTEX,{"derivedFrom":[subQ6,subQ0]});Q1=makeQuery(id+"F0.imprint","IMPRINT",FACE,{"disambiguationData":[TD([[makeQuery(id+"F0.imprint","IMPRINT",EDGE,{"disambiguationData":[TD([[subQ9,-1.0]])],"derivedFrom":subQ6}),-1.0]])]});}
            var Q2;
            {var subQ0=sQuery(id+"F0.wireOp",EDGE,"E34");var subQ1=sQuery(id+"F0.wireOp",EDGE,"E7");var subQ2=makeQuery(id+"F0.imprint","INTERSECT",VERTEX,{"derivedFrom":[subQ1,subQ0]});Q2=makeQuery(id+"F0.imprint","IMPRINT",FACE,{"disambiguationData":[TD([[makeQuery(id+"F0.imprint","IMPRINT",EDGE,{"disambiguationData":[TD([[subQ2,-1.0]])],"derivedFrom":subQ1}),1.0]])]});}
            var Q3;
            {var subQ5=sQuery(id+"F0.wireOp",EDGE,"E36");Q3=makeQuery(id+"F0.imprint","IMPRINT",FACE,{"disambiguationData":[TD([[makeQuery(id+"F0.imprint","IMPRINT",EDGE,{"derivedFrom":subQ5}),1.0]])]});}
            var Q4;
            {var subQ5=sQuery(id+"F0.wireOp",EDGE,"E39");Q4=makeQuery(id+"F0.imprint","IMPRINT",FACE,{"disambiguationData":[TD([[makeQuery(id+"F0.imprint","IMPRINT",EDGE,{"derivedFrom":subQ5}),-1.0]])]});}
            var Q5;
            {var subQ0=sQuery(id+"F0.wireOp",EDGE,"E33");var subQ1=sQuery(id+"F0.wireOp",EDGE,"E2.left");var subQ2=makeQuery(id+"F0.imprint","INTERSECT",VERTEX,{"derivedFrom":[subQ1,subQ0]});Q5=makeQuery(id+"F0.imprint","IMPRINT",FACE,{"disambiguationData":[TD([[makeQuery(id+"F0.imprint","IMPRINT",EDGE,{"disambiguationData":[TD([[subQ2,-1.0]])],"derivedFrom":subQ1}),-1.0]])]});}
            var Q6;
            {var subQ0=sQuery(id+"F0.wireOp",EDGE,"E30.bottom");var subQ1=sQuery(id+"F0.wireOp",EDGE,"E2.left");var subQ2=makeQuery(id+"F0.imprint","INTERSECT",VERTEX,{"derivedFrom":[subQ1,subQ0]});Q6=makeQuery(id+"F0.imprint","IMPRINT",FACE,{"disambiguationData":[TD([[makeQuery(id+"F0.imprint","IMPRINT",EDGE,{"disambiguationData":[TD([[subQ2,-1.0]])],"derivedFrom":subQ1}),1.0]])]});}
            var Q7;
            {var subQ0=sQuery(id+"F0.wireOp",EDGE,"E30.bottom");var subQ1=sQuery(id+"F0.wireOp",EDGE,"E2.left");var subQ2=makeQuery(id+"F0.imprint","INTERSECT",VERTEX,{"derivedFrom":[subQ1,subQ0]});Q7=makeQuery(id+"F0.imprint","IMPRINT",FACE,{"disambiguationData":[TD([[makeQuery(id+"F0.imprint","IMPRINT",EDGE,{"disambiguationData":[TD([[subQ2,-1.0]])],"derivedFrom":subQ1}),-1.0]])]});}
            var Q8;
            {var subQ0=sQuery(id+"F0.wireOp",EDGE,"E37");var subQ6=sQuery(id+"F0.wireOp",EDGE,"E20.MirrorCS");var subQ9=makeQuery(id+"F0.imprint","INTERSECT",VERTEX,{"derivedFrom":[subQ6,subQ0]});Q8=makeQuery(id+"F0.imprint","IMPRINT",FACE,{"disambiguationData":[TD([[makeQuery(id+"F0.imprint","IMPRINT",EDGE,{"disambiguationData":[TD([[subQ9,-1.0]])],"derivedFrom":subQ6}),1.0]])]});}
            var Q9;
            {var subQ0=sQuery(id+"F0.wireOp",EDGE,"E37");var subQ1=sQuery(id+"F0.wireOp",EDGE,"E20.MirrorCS");var subQ2=makeQuery(id+"F0.imprint","INTERSECT",VERTEX,{"derivedFrom":[subQ1,subQ0]});Q9=makeQuery(id+"F0.imprint","IMPRINT",FACE,{"disambiguationData":[TD([[makeQuery(id+"F0.imprint","IMPRINT",EDGE,{"disambiguationData":[TD([[subQ2,-1.0]])],"derivedFrom":subQ1}),-1.0]])]});}
            extrude(context, id + "F6", {"entities" : qUnion([Q0, Q1, Q2, Q3, Q4, Q5, Q6, Q7, Q8, Q9]), "operationType" : NewBodyOperationType.ADD, "depth" : 10 * mm, "offsetDistance" : 25 * mm});
        }
        {
            var Q0;
            {var subQ0=sQuery(id+"F0.wireOp",EDGE,"E30.right");var subQ1=sQuery(id+"F0.wireOp",EDGE,"E0.right");Q0=makeQuery(id+"F3.boolean.opBoolean","MERGE",FACE,{"derivedFrom":[makeQuery(id+"F1.opExtrude","SWEPT_FACE",FACE,{"disambiguationData":[OSD([subQ1,subQ0])]}),makeQuery(id+"F3.opExtrude","SWEPT_FACE",FACE,{"disambiguationData":[OSD([subQ1,subQ0])]})]});}
            var sketch = newSketch(context, id + "F7", { "sketchPlane" : qUnion([Q0])});
            skLineSegment(sketch, "E42.bottom", {"start": v(-40, -2.5) * mm, "end": v(45, -2.5) * mm});
            skLineSegment(sketch, "E42.top", {"start": v(-40, -7.5) * mm, "end": v(45, -7.5) * mm});
            skLineSegment(sketch, "E42.left", {"start": v(-42.5, -5) * mm, "end": v(-42.5, -5) * mm});
            skLineSegment(sketch, "E42.right", {"start": v(47.5, -5) * mm, "end": v(47.5, -5) * mm});
            skPoint(sketch, "E43.visualSharp", {"position": v(-42.5, -7.5) * mm});
            skArc(sketch, "E43.filletArc", {"start": v(-42.5, -5) * mm, "mid": v(-41.77, -6.77) * mm, "end": v(-40, -7.5) * mm});
            skPoint(sketch, "E44.visualSharp", {"position": v(-42.5, -2.5) * mm});
            skArc(sketch, "E44.filletArc", {"start": v(-40, -2.5) * mm, "mid": v(-41.77, -3.23) * mm, "end": v(-42.5, -5) * mm});
            skPoint(sketch, "E45.visualSharp", {"position": v(47.5, -2.5) * mm});
            skArc(sketch, "E45.filletArc", {"start": v(47.5, -5) * mm, "mid": v(46.77, -3.23) * mm, "end": v(45, -2.5) * mm});
            skPoint(sketch, "E46.visualSharp", {"position": v(47.5, -7.5) * mm});
            skArc(sketch, "E46.filletArc", {"start": v(45, -7.5) * mm, "mid": v(46.77, -6.77) * mm, "end": v(47.5, -5) * mm});
            skSolve(sketch);
        }
        {
            var Q0;
            Q0=makeQuery(id+"F7.imprint","IMPRINT",FACE,{"disambiguationData":[TD([[makeQuery(id+"F7.imprint","IMPRINT",EDGE,{"derivedFrom":sQuery(id+"F7.wireOp",EDGE,"E42.bottom")}),-1.0]])]});
            extrude(context, id + "F8", {"entities" : qUnion([Q0]), "operationType" : NewBodyOperationType.REMOVE, "oppositeDirection" : true, "depth" : 25 * mm, "offsetDistance" : 25 * mm});
        }
        {
            var Q0;
            {var subQ0=sQuery(id+"F0.wireOp",EDGE,"E30.left");var subQ1=sQuery(id+"F0.wireOp",EDGE,"E0.left");Q0=makeQuery(id+"F5.boolean.opBoolean","MERGE",FACE,{"derivedFrom":[makeQuery(id+"F4.opExtrude","SWEPT_FACE",FACE,{"disambiguationData":[OSD([subQ1,subQ0])]}),makeQuery(id+"F5.opExtrude","SWEPT_FACE",FACE,{"disambiguationData":[OSD([subQ1,subQ0])]})]});}
            var sketch = newSketch(context, id + "F9", { "sketchPlane" : qUnion([Q0])});
            skLineSegment(sketch, "E47.bottom", {"start": v(10, -2.5) * mm, "end": v(45, -2.5) * mm});
            skLineSegment(sketch, "E47.top", {"start": v(10, -7.5) * mm, "end": v(45, -7.5) * mm});
            skLineSegment(sketch, "E47.left", {"start": v(7.5, -5) * mm, "end": v(7.5, -5) * mm});
            skLineSegment(sketch, "E47.right", {"start": v(47.5, -5) * mm, "end": v(47.5, -5) * mm});
            skPoint(sketch, "E48.visualSharp", {"position": v(7.5, -7.5) * mm});
            skArc(sketch, "E48.filletArc", {"start": v(7.5, -5) * mm, "mid": v(8.23, -6.77) * mm, "end": v(10, -7.5) * mm});
            skPoint(sketch, "E49.visualSharp", {"position": v(7.5, -2.5) * mm});
            skArc(sketch, "E49.filletArc", {"start": v(10, -2.5) * mm, "mid": v(8.23, -3.23) * mm, "end": v(7.5, -5) * mm});
            skPoint(sketch, "E50.visualSharp", {"position": v(47.5, -2.5) * mm});
            skArc(sketch, "E50.filletArc", {"start": v(47.5, -5) * mm, "mid": v(46.77, -3.23) * mm, "end": v(45, -2.5) * mm});
            skPoint(sketch, "E51.visualSharp", {"position": v(47.5, -7.5) * mm});
            skArc(sketch, "E51.filletArc", {"start": v(45, -7.5) * mm, "mid": v(46.77, -6.77) * mm, "end": v(47.5, -5) * mm});
            skSolve(sketch);
        }
        {
            var Q0;
            Q0=makeQuery(id+"F9.imprint","IMPRINT",FACE,{"disambiguationData":[TD([[makeQuery(id+"F9.imprint","IMPRINT",EDGE,{"derivedFrom":sQuery(id+"F9.wireOp",EDGE,"E47.bottom")}),-1.0]])]});
            extrude(context, id + "F10", {"entities" : qUnion([Q0]), "operationType" : NewBodyOperationType.REMOVE, "oppositeDirection" : true, "depth" : 25 * mm, "offsetDistance" : 25 * mm});
        }
    });
